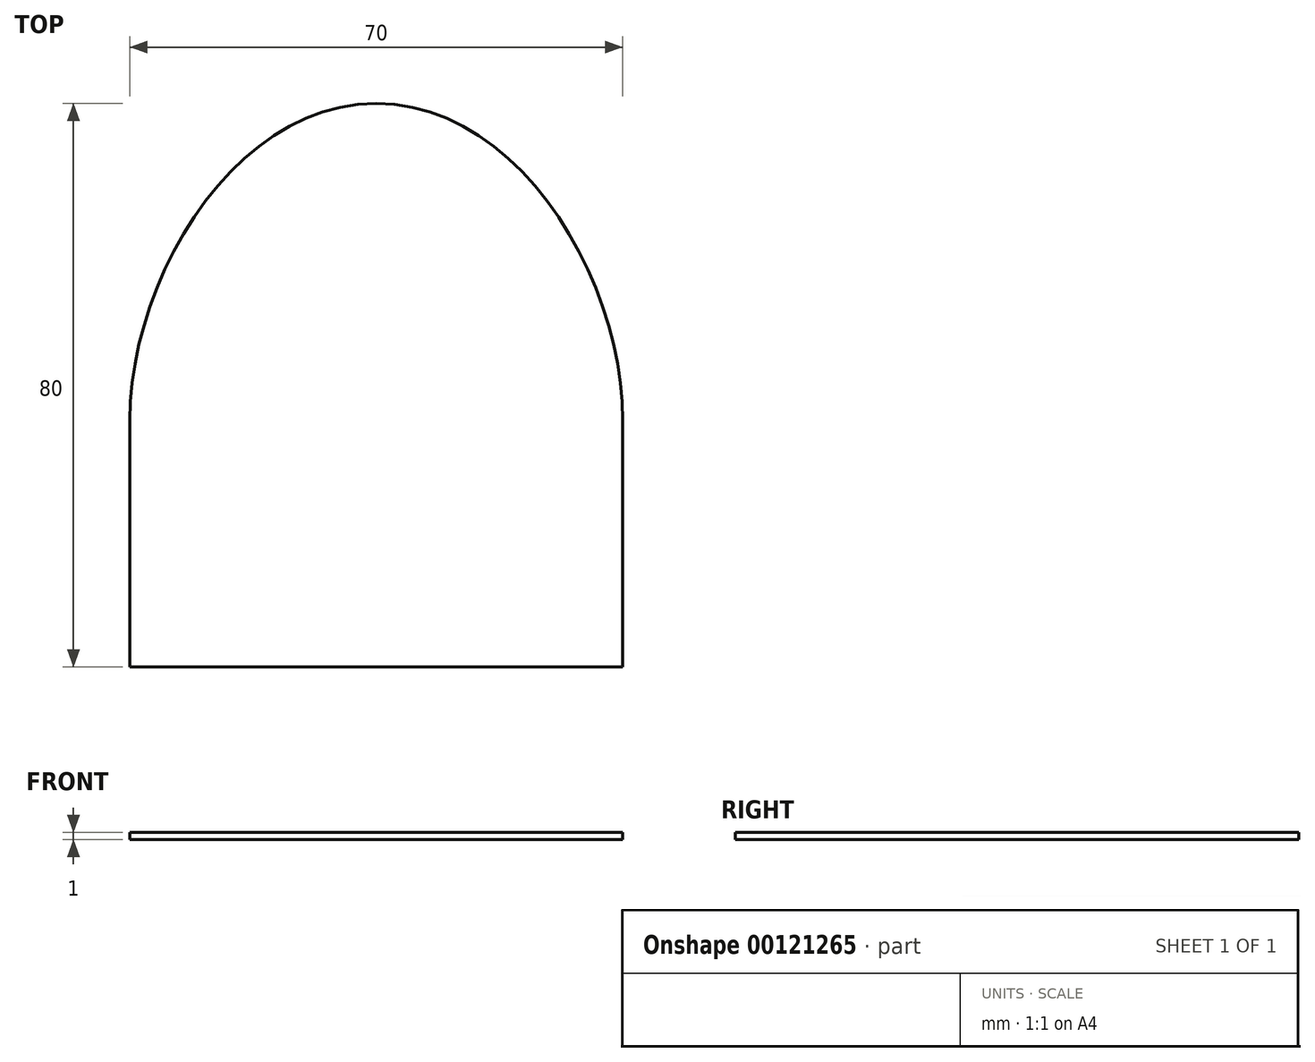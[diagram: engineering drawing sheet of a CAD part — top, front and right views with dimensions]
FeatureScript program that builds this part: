
annotation { "Feature Type Name" : "Feature", "Feature Type Description" : "" }
export const myFeature = defineFeature(function(context is Context, id is Id, definition is map)
    precondition{}
    {
        {
            var Q0;
            Q0=qCreatedBy(makeId("Top.planeOp"),FACE);
            var sketch = newSketch(context, id + "F0", { "sketchPlane" : qUnion([Q0])});
            skLineSegment(sketch, "E0.top", {"start": v(-35, -35) * mm, "end": v(35, -35) * mm});
            skPoint(sketch, "E0.middle", {"position": v(0, 13.14) * mm});
            skPoint(sketch, "E1", {"position": v(0, 0) * mm});
            skCircle(sketch, "E2", {"center": v(0, 0) * mm, "radius": 35 * mm});
            skPoint(sketch, "E3.visualSharp", {"position": v(-35, -35) * mm});
            skPoint(sketch, "E4.visualSharp", {"position": v(35, -35) * mm});
            skPoint(sketch, "E5", {"position": v(-35, 0) * mm});
            skPoint(sketch, "E6", {"position": v(35, 0) * mm});
            skFitSpline(sketch, "E7", {"points": [v(0, 45) * mm, v(-35, 0) * mm], "startDerivative": vector(-60.6, 0) * mm, "endDerivative": vector(0, -60.15) * mm});
            skLineSegment(sketch, "E8", {"start": v(-35, 0) * mm, "end": v(-35, -35) * mm});
            skLineSegment(sketch, "E9", {"start": v(35, 0) * mm, "end": v(35, -35) * mm});
            skFitSpline(sketch, "E10.MirrorCS", {"points": [v(0, 45) * mm, v(35, 0) * mm], "startDerivative": vector(60.6, 0) * mm, "endDerivative": vector(0, -60.15) * mm});
            skFitSpline(sketch, "E11.0", {"points": [v(0, 37) * mm, v(-0.85, 37) * mm, v(-2.51, 36.87) * mm, v(-4.95, 36.3) * mm, v(-7.36, 35.37) * mm, v(-10.54, 33.64) * mm, v(-14.42, 30.55) * mm, v(-18.67, 25.54) * mm, v(-22.24, 19.56) * mm, v(-24.95, 13) * mm, v(-26.62, 6.3) * mm, v(-27, 2.01) * mm, v(-27, 0) * mm]});
            skPoint(sketch, "E12", {"position": v(0, 37) * mm});
            skPoint(sketch, "E13", {"position": v(-7.77, 35.11) * mm});
            skPoint(sketch, "E14", {"position": v(-14.26, 30.43) * mm});
            skPoint(sketch, "E15", {"position": v(-19.34, 24.24) * mm});
            skPoint(sketch, "E16", {"position": v(-23.15, 17.21) * mm});
            skPoint(sketch, "E17", {"position": v(-25.74, 9.64) * mm});
            skLineSegment(sketch, "E18", {"start": v(-27, 0) * mm, "end": v(-27, -35) * mm});
            skPoint(sketch, "E19", {"position": v(-26.96, 1.74) * mm});
            skPoint(sketch, "E20", {"position": v(-25.02, 3.05) * mm});
            skSolve(sketch);
        }
        {
            var Q0;
            Q0 = qSketchRegion(id + "F0", true);
            extrude(context, id + "F1", {"entities" : qUnion([Q0]), "depth" : 1 * mm});
        }
    });
